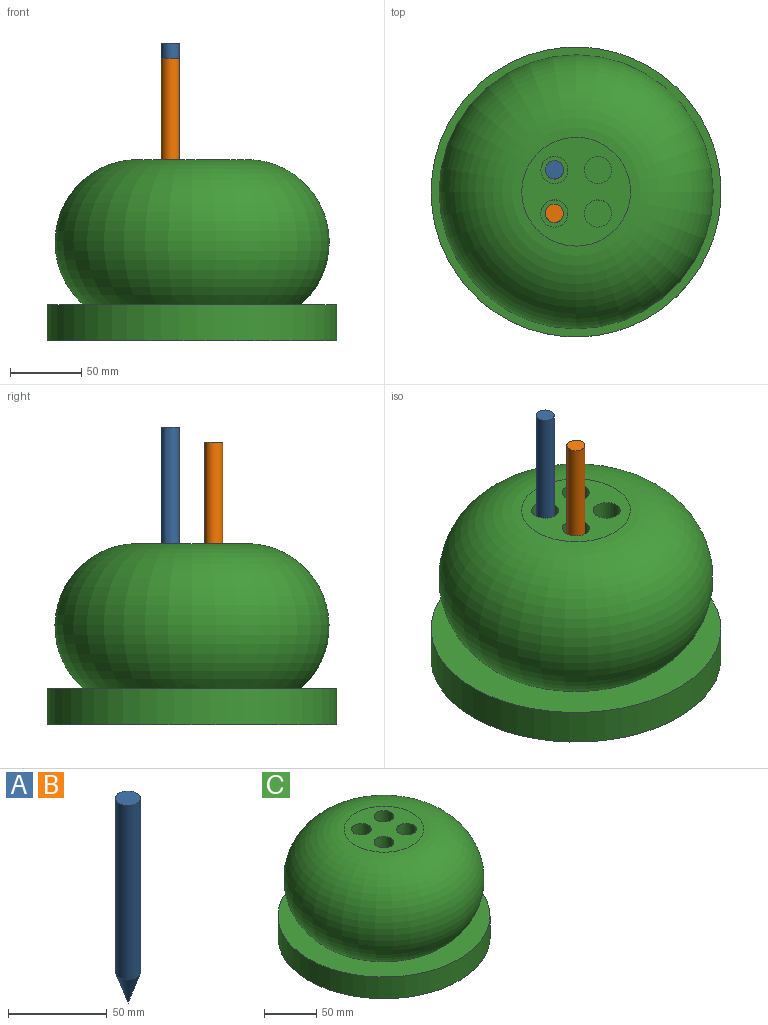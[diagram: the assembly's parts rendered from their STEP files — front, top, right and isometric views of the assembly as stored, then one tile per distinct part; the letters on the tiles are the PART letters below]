
ASSEMBLY  parts=3 mates=2
PART A: 3 faces, bbox 12.7x12.7x127 mm
  f0: cylinder r=6.35mm len=107.95mm, axis (0,0,-1), area 4307mm2, adj f1,f2
  f1: plane 12.7x12.7mm, normal (0,0,1), area 126.7mm2, adj f0
  f2: cone r=6.35mm half-angle=18.4deg, axis (0,0,1), area 400.6mm2, adj f0
PART B: same geometry as A
PART C: 113 faces, bbox 203.2x203.2x127 mm
  f0: plane 203.2x203.2mm, normal (0,0,-1), area 30855.4mm2, adj f4,f13,f14,f15,f16,f17,f18,f19
  f1: plane 76.2x76.2mm, normal (0,0,1), area 3420.3mm2, adj f2,f5,f7,f9,f11
  f2: torus R=38.1mm, axis (0,0,-1), area 70613.9mm2, adj f1,f3
  f3: plane 203.2x203.2mm, normal (0,0,1), area 14187.8mm2, adj f2,f4
  f4: cylinder r=101.6mm len=203.2mm, axis (0,0,-1), area 16214.6mm2, adj f0,f3
  f5: cylinder r=9.53mm len=76.2mm, axis (0,0,1), area 4560.4mm2, adj f1,f6
  f6: plane 19.05x19.05mm, normal (0,0,1), area 285mm2, adj f5
  f7: cylinder r=9.53mm len=76.2mm, axis (0,0,1), area 4560.4mm2, adj f1,f8
  f8: plane 19.05x19.05mm, normal (0,0,1), area 285mm2, adj f7
  f9: cylinder r=9.53mm len=76.2mm, axis (0,0,1), area 4560.4mm2, adj f1,f10
  f10: plane 19.05x19.05mm, normal (0,0,1), area 285mm2, adj f9
  f11: cylinder r=9.53mm len=76.2mm, axis (0,0,1), area 4560.4mm2, adj f1,f12
  f12: plane 19.05x19.05mm, normal (0,0,1), area 285mm2, adj f11
  f13: extruded ~9.51x3.05mm, area 25.9mm2, adj f0,f14,f28,f29
  f14: extruded ~8.48x3.45mm, area 24mm2, adj f0,f13,f15,f29
  f15: extruded ~8.61x3.38mm, area 24.2mm2, adj f0,f14,f16,f29
  f16: extruded ~9.54x3.03mm, area 26mm2, adj f0,f15,f17,f29
  f17: extruded ~9.61x3.02mm, area 26.2mm2, adj f0,f16,f18,f29
  f18: extruded ~8.59x3.4mm, area 24.2mm2, adj f0,f17,f19,f29
  f19: extruded ~8.5x3.46mm, area 24.1mm2, adj f0,f18,f28,f29
  f20: extruded ~7.69x2.54mm, area 20.7mm2, adj f21,f27,f29,f30
  f21: extruded ~6.36x2.65mm, area 18.1mm2, adj f20,f22,f29,f30
  f22: extruded ~6.3x2.63mm, area 17.9mm2, adj f21,f23,f29,f30
  f23: extruded ~7.71x2.54mm, area 20.7mm2, adj f22,f24,f29,f30
  f24: extruded ~7.77x2.54mm, area 20.9mm2, adj f23,f25,f29,f30
  f25: extruded ~6.32x2.64mm, area 18mm2, adj f24,f26,f29,f30
  f26: extruded ~6.33x2.65mm, area 18mm2, adj f25,f27,f29,f30
  f27: extruded ~7.76x2.54mm, area 20.9mm2, adj f20,f26,f29,f30
  f28: extruded ~9.51x3.06mm, area 26mm2, adj f0,f13,f19,f29
  f29: plane 25.93x23.17mm, normal (0,0,-1), area 200.7mm2, adj f13,f14,f15,f16,f17,f18,f19,f20
  f30: plane 20.74x16.97mm, normal (0,0,-1), area 291.8mm2, adj f20,f21,f22,f23,f24,f25,f26,f27
  f31: extruded ~4.2x2.54mm, area 11.6mm2, adj f0,f32,f55,f56
  f32: extruded ~5.45x3.03mm, area 16mm2, adj f0,f31,f33,f56
  f33: extruded ~3.51x2.54mm, area 9.7mm2, adj f0,f32,f34,f56
  f34: extruded ~2.54x1.63mm, area 5.7mm2, adj f0,f33,f35,f56
  f35: extruded ~2.54x2.14mm, area 5.6mm2, adj f0,f34,f36,f56
  f36: extruded ~2.77x2.54mm, area 8.1mm2, adj f0,f35,f37,f56
  f37: extruded ~3.64x2.54mm, area 9.7mm2, adj f0,f36,f38,f56
  f38: extruded ~6.06x2.54mm, area 15.9mm2, adj f0,f37,f39,f56
  f39: plane 2.55x2.54mm, normal (-0.94,-0.34,0), area 6.9mm2, adj f0,f38,f40,f56
  f40: extruded ~6.91x2.54mm, area 18mm2, adj f0,f39,f41,f56
  f41: extruded ~5.79x2.54mm, area 15.6mm2, adj f0,f40,f42,f56
  f42: extruded ~4.63x2.54mm, area 13.5mm2, adj f0,f41,f43,f56
  f43: extruded ~4.5x2.54mm, area 12.3mm2, adj f0,f42,f44,f56
  f44: extruded ~5.02x2.98mm, area 15mm2, adj f0,f43,f45,f56
  f45: extruded ~3.75x2.54mm, area 10.4mm2, adj f0,f44,f46,f56
  f46: extruded ~2.54x1.76mm, area 6mm2, adj f0,f45,f47,f56
  f47: extruded ~2.54x2.14mm, area 5.7mm2, adj f0,f46,f48,f56
  f48: extruded ~3.1x2.54mm, area 9.1mm2, adj f0,f47,f49,f56
  f49: extruded ~4.41x2.54mm, area 11.7mm2, adj f0,f48,f50,f56
  f50: extruded ~3.62x2.54mm, area 9.3mm2, adj f0,f49,f51,f56
  f51: extruded ~3.38x2.54mm, area 9mm2, adj f0,f50,f52,f56
  f52: plane 2.82x2.54mm, normal (1,0,0), area 7.2mm2, adj f0,f51,f53,f56
  f53: extruded ~6.89x2.54mm, area 17.9mm2, adj f0,f52,f54,f56
  f54: extruded ~6.55x2.54mm, area 17.6mm2, adj f0,f53,f55,f56
  f55: extruded ~5.19x2.54mm, area 15.1mm2, adj f0,f31,f54,f56
  f56: plane 25.89x15.85mm, normal (0,0,-1), area 146.8mm2, adj f31,f32,f33,f34,f35,f36,f37,f38
  f57: plane 14.04x2.54mm, normal (0,-1,0), area 35.7mm2, adj f0,f58,f62,f63
  f58: plane 2.65x2.54mm, normal (-1,0,0), area 6.7mm2, adj f0,f57,f59,f63
  f59: plane 11.11x2.54mm, normal (0,1,0), area 28.2mm2, adj f0,f58,f60,f63
  f60: plane 22.53x2.54mm, normal (-1,0,0), area 57.2mm2, adj f0,f59,f61,f63
  f61: plane 2.93x2.54mm, normal (0,1,0), area 7.4mm2, adj f0,f60,f62,f63
  f62: plane 25.19x2.54mm, normal (1,0,0), area 64mm2, adj f0,f57,f61,f63
  f63: plane 25.19x14.04mm, normal (0,0,-1), area 103.2mm2, adj f57,f58,f59,f60,f61,f62
  f64: plane 16.19x5.75mm, normal (0.94,0.33,0), area 43.7mm2, adj f0,f65,f72,f73
  f65: extruded ~5.56x2.54mm, area 14.7mm2, adj f0,f64,f66,f73
  f66: extruded ~5.46x2.54mm, area 14.5mm2, adj f0,f65,f67,f73
  f67: plane 16.29x5.79mm, normal (-0.94,0.33,0), area 43.9mm2, adj f0,f66,f68,f73
  f68: plane 3.1x2.54mm, normal (0,1,0), area 7.9mm2, adj f0,f67,f69,f73
  f69: plane 25.19x9.03mm, normal (0.94,-0.34,0), area 68mm2, adj f0,f68,f70,f73
  f70: plane 2.89x2.54mm, normal (0,-1,0), area 7.4mm2, adj f0,f69,f71,f73
  f71: plane 25.19x9.07mm, normal (-0.94,-0.34,0), area 68mm2, adj f0,f70,f72,f73
  f72: plane 3.15x2.54mm, normal (0,1,0), area 8mm2, adj f0,f64,f71,f73
  f73: plane 25.19x21mm, normal (0,0,-1), area 146.9mm2, adj f64,f65,f66,f67,f68,f69,f70,f71
  f74: extruded ~9.51x3.05mm, area 25.9mm2, adj f0,f75,f89,f90
  f75: extruded ~8.48x3.45mm, area 24mm2, adj f0,f74,f76,f90
  f76: extruded ~8.61x3.38mm, area 24.2mm2, adj f0,f75,f77,f90
  f77: extruded ~9.54x3.03mm, area 26mm2, adj f0,f76,f78,f90
  f78: extruded ~9.61x3.02mm, area 26.2mm2, adj f0,f77,f79,f90
  f79: extruded ~8.59x3.4mm, area 24.2mm2, adj f0,f78,f80,f90
  f80: extruded ~8.5x3.46mm, area 24.1mm2, adj f0,f79,f89,f90
  f81: extruded ~7.69x2.54mm, area 20.7mm2, adj f82,f88,f90,f91
  f82: extruded ~6.36x2.65mm, area 18.1mm2, adj f81,f83,f90,f91
  f83: extruded ~6.3x2.63mm, area 17.9mm2, adj f82,f84,f90,f91
  f84: extruded ~7.71x2.54mm, area 20.7mm2, adj f83,f85,f90,f91
  f85: extruded ~7.77x2.54mm, area 20.9mm2, adj f84,f86,f90,f91
  f86: extruded ~6.32x2.64mm, area 18mm2, adj f85,f87,f90,f91
  f87: extruded ~6.33x2.65mm, area 18mm2, adj f86,f88,f90,f91
  f88: extruded ~7.76x2.54mm, area 20.9mm2, adj f81,f87,f90,f91
  f89: extruded ~9.51x3.06mm, area 26mm2, adj f0,f74,f80,f90
  f90: plane 25.93x23.17mm, normal (0,0,-1), area 200.7mm2, adj f74,f75,f76,f77,f78,f79,f80,f81
  f91: plane 20.74x16.97mm, normal (0,0,-1), area 291.8mm2, adj f81,f82,f83,f84,f85,f86,f87,f88
  f92: plane 2.62x2.54mm, normal (1,0,0), area 6.7mm2, adj f0,f93,f111,f112
  f93: plane 5.63x2.54mm, normal (0,-1,0), area 14.3mm2, adj f0,f92,f94,f112
  f94: plane 7.75x2.54mm, normal (1,0,0), area 19.7mm2, adj f0,f93,f95,f112
  f95: extruded ~5.12x2.54mm, area 13.1mm2, adj f0,f94,f96,f112
  f96: extruded ~7.31x2.64mm, area 20.3mm2, adj f0,f95,f97,f112
  f97: extruded ~7.73x2.54mm, area 21.1mm2, adj f0,f96,f98,f112
  f98: extruded ~7.6x2.59mm, area 20.9mm2, adj f0,f97,f99,f112
  f99: extruded ~7.18x2.74mm, area 20.1mm2, adj f0,f98,f100,f112
  f100: extruded ~6.57x2.54mm, area 17.2mm2, adj f0,f99,f101,f112
  f101: plane 2.59x2.54mm, normal (-0.92,-0.4,0), area 7.2mm2, adj f0,f100,f102,f112
  f102: extruded ~7.51x2.54mm, area 19.6mm2, adj f0,f101,f103,f112
  f103: extruded ~6.94x2.54mm, area 18.2mm2, adj f0,f102,f104,f112
  f104: extruded ~4.54x4.51mm, area 16.5mm2, adj f0,f103,f105,f112
  f105: extruded ~6.88x2.54mm, area 18.1mm2, adj f0,f104,f106,f112
  f106: extruded ~9.53x3.19mm, area 26.2mm2, adj f0,f105,f107,f112
  f107: extruded ~8.9x3.4mm, area 24.9mm2, adj f0,f106,f108,f112
  f108: extruded ~4.79x2.54mm, area 12.2mm2, adj f0,f107,f109,f112
  f109: extruded ~4.07x2.54mm, area 10.6mm2, adj f0,f108,f110,f112
  f110: plane 12.25x2.54mm, normal (-1,0,0), area 31.1mm2, adj f0,f109,f111,f112
  f111: plane 8.56x2.54mm, normal (0,1,0), area 21.7mm2, adj f0,f92,f110,f112
  f112: plane 25.89x20.95mm, normal (0,0,-1), area 192mm2, adj f92,f93,f94,f95,f96,f97,f98,f99
PLACE A t=(-40.02,58.01,81.61)mm
PLACE B t=(-40.02,27.53,70.88)mm
PLACE C t=(-24.78,42.77,0)mm fixed
MATE slider A.f0 <-> C.f5  axis (0,0,1) through (-40.02,58.01,208.61)mm
MATE slider B.f0 <-> C.f11  axis (0,0,1) through (-40.02,27.53,197.88)mm
